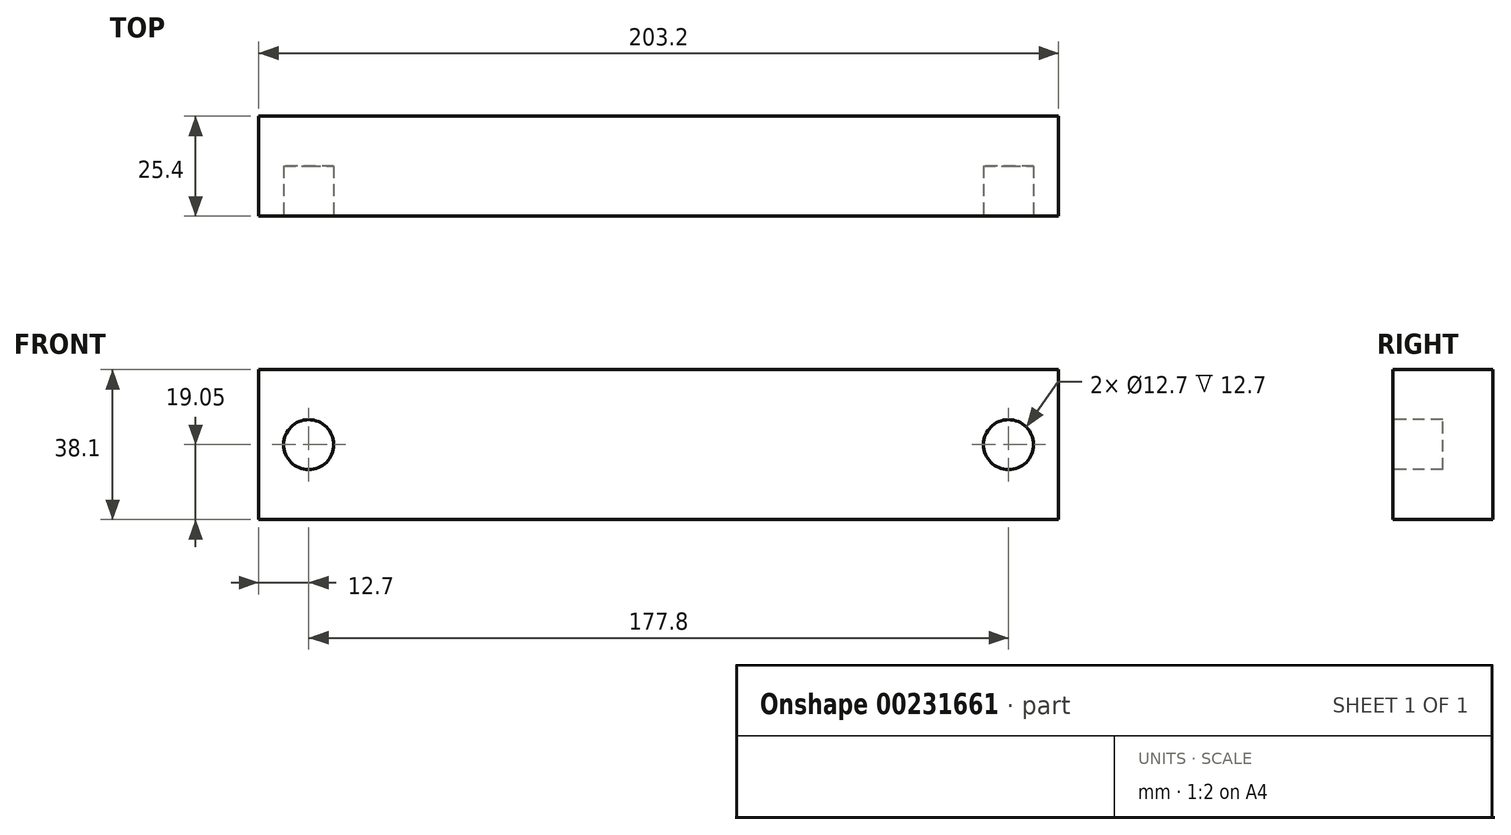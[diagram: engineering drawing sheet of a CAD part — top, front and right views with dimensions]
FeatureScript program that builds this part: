
annotation { "Feature Type Name" : "Feature", "Feature Type Description" : "" }
export const myFeature = defineFeature(function(context is Context, id is Id, definition is map)
    precondition{}
    {
        {
            var Q0;
            Q0=qCreatedBy(makeId("Front.planeOp"),FACE);
            var sketch = newSketch(context, id + "F0", { "sketchPlane" : qUnion([Q0])});
            skLineSegment(sketch, "E0.bottom", {"start": v(-101.6, 19.05) * mm, "end": v(101.6, 19.05) * mm});
            skLineSegment(sketch, "E0.top", {"start": v(-101.6, -19.05) * mm, "end": v(101.6, -19.05) * mm});
            skLineSegment(sketch, "E0.left", {"start": v(-101.6, 19.05) * mm, "end": v(-101.6, -19.05) * mm});
            skLineSegment(sketch, "E0.right", {"start": v(101.6, 19.05) * mm, "end": v(101.6, -19.05) * mm});
            skPoint(sketch, "E0.middle", {"position": v(0, 0) * mm});
            skSolve(sketch);
        }
        {
            var Q0;
            Q0 = qSketchRegion(id + "F0", true);
            extrude(context, id + "F1", {"entities" : qUnion([Q0]), "depth" : 25.4 * mm});
        }
        {
            var Q0;
            Q0=makeQuery(id+"F1.opExtrude","CAP_FACE",FACE,{"disambiguationData":[OSD([sQuery(id+"F0.wireOp",EDGE,"E0.bottom"),sQuery(id+"F0.wireOp",EDGE,"E0.top"),sQuery(id+"F0.wireOp",EDGE,"E0.left"),sQuery(id+"F0.wireOp",EDGE,"E0.right")])],"isStart":false});
            var sketch = newSketch(context, id + "F2", { "sketchPlane" : qUnion([Q0])});
            skLineSegment(sketch, "E1", {"start": v(-88.9, 19.05) * mm, "end": v(-88.9, -19.05) * mm, "construction": true});
            skLineSegment(sketch, "E2", {"start": v(-88.9, -19.05) * mm, "end": v(88.9, -19.05) * mm, "construction": true});
            skLineSegment(sketch, "E3", {"start": v(88.9, -19.05) * mm, "end": v(88.9, 19.05) * mm, "construction": true});
            skCircle(sketch, "E4", {"center": v(-88.9, 0) * mm, "radius": 6.35 * mm});
            skCircle(sketch, "E5", {"center": v(88.9, 0) * mm, "radius": 6.35 * mm});
            skSolve(sketch);
        }
        {
            var Q0;
            Q0 = qSketchRegion(id + "F2", true);
            extrude(context, id + "F3", {"entities" : qUnion([Q0]), "operationType" : NewBodyOperationType.REMOVE, "oppositeDirection" : true, "depth" : 12.7 * mm});
        }
    });
